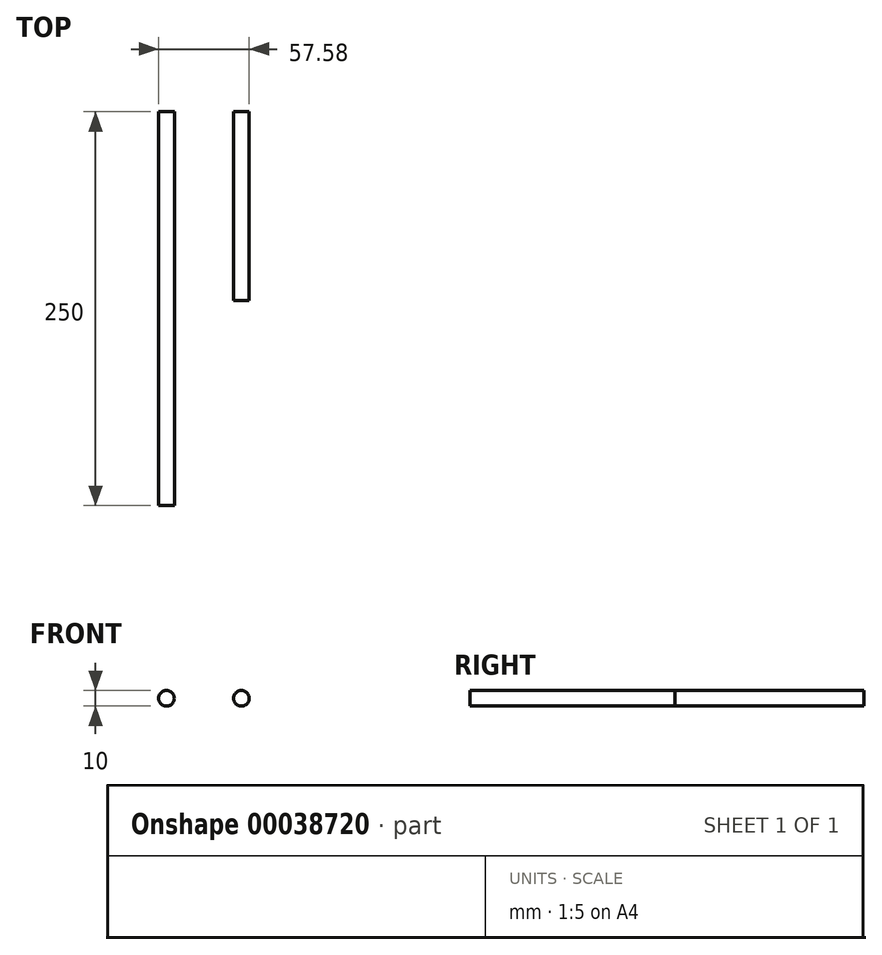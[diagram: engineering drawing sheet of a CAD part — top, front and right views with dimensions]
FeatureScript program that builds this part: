
annotation { "Feature Type Name" : "Feature", "Feature Type Description" : "" }
export const myFeature = defineFeature(function(context is Context, id is Id, definition is map)
    precondition{}
    {
        {
            var Q0;
            Q0=qCreatedBy(makeId("Front.planeOp"),FACE);
            var sketch = newSketch(context, id + "F0", { "sketchPlane" : qUnion([Q0])});
            skCircle(sketch, "E0", {"center": v(-28.2, 0) * mm, "radius": 5 * mm});
            skSolve(sketch);
        }
        {
            var Q0;
            Q0=makeQuery(id+"F0.imprint","IMPRINT",FACE,{"disambiguationData":[TD([[makeQuery(id+"F0.imprint","IMPRINT",EDGE,{"derivedFrom":sQuery(id+"F0.wireOp",EDGE,"E0")}),1.0]])]});
            extrude(context, id + "F1", {"entities" : qUnion([Q0]), "depth" : 250 * mm});
        }
        {
            var Q0;
            Q0=qCreatedBy(makeId("Front.planeOp"),FACE);
            var sketch = newSketch(context, id + "F2", { "sketchPlane" : qUnion([Q0])});
            skCircle(sketch, "E1", {"center": v(19.38, 0) * mm, "radius": 5 * mm});
            skSolve(sketch);
        }
        {
            var Q0;
            Q0=makeQuery(id+"F2.imprint","IMPRINT",FACE,{"disambiguationData":[TD([[makeQuery(id+"F2.imprint","IMPRINT",EDGE,{"derivedFrom":sQuery(id+"F2.wireOp",EDGE,"E1")}),1.0]])]});
            extrude(context, id + "F3", {"entities" : qUnion([Q0]), "depth" : 120 * mm});
        }
    });
